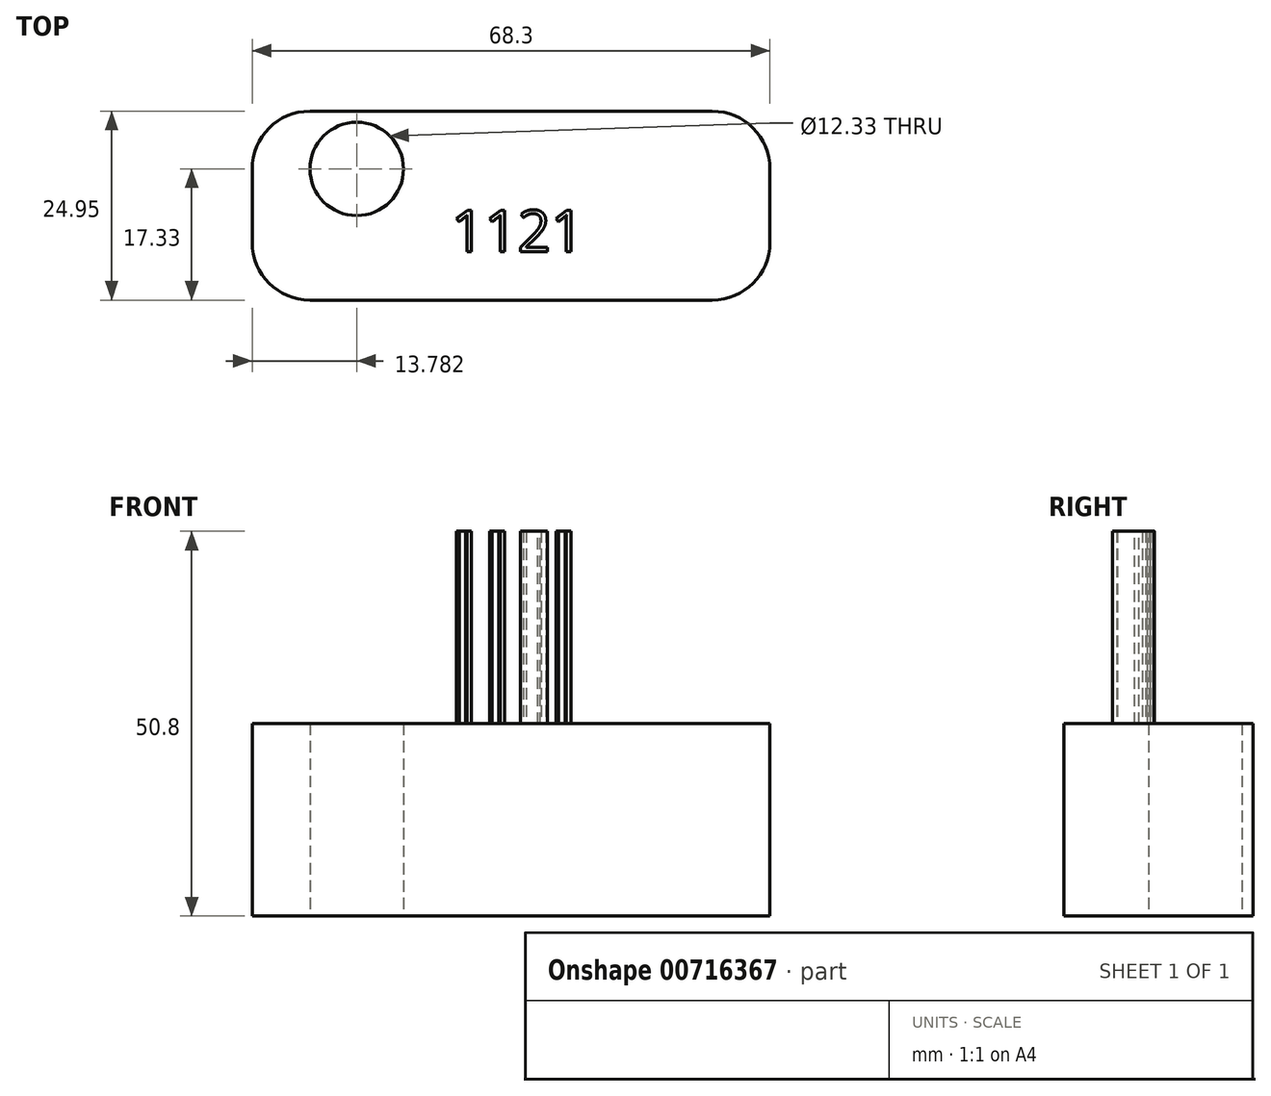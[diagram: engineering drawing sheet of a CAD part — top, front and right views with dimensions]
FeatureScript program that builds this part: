
annotation { "Feature Type Name" : "Feature", "Feature Type Description" : "" }
export const myFeature = defineFeature(function(context is Context, id is Id, definition is map)
    precondition{}
    {
        {
            var Q0;
            Q0=qCreatedBy(makeId("Top.planeOp"),FACE);
            var sketch = newSketch(context, id + "F0", { "sketchPlane" : qUnion([Q0])});
            skLineSegment(sketch, "E0.bottom", {"start": v(-7.62, 33.82) * mm, "end": v(-60.68, 33.82) * mm});
            skLineSegment(sketch, "E0.top", {"start": v(-7.62, 8.87) * mm, "end": v(-60.68, 8.87) * mm});
            skLineSegment(sketch, "E0.left", {"start": v(0, 26.2) * mm, "end": v(0, 16.49) * mm});
            skLineSegment(sketch, "E0.right", {"start": v(-68.3, 26.2) * mm, "end": v(-68.3, 16.49) * mm});
            skPoint(sketch, "E0.middle", {"position": v(-34.15, 21.34) * mm});
            skPoint(sketch, "E1.visualSharp", {"position": v(0, 33.82) * mm});
            skArc(sketch, "E1.filletArc", {"start": v(0, 26.2) * mm, "mid": v(-2.23, 31.59) * mm, "end": v(-7.62, 33.82) * mm});
            skPoint(sketch, "E2.visualSharp", {"position": v(0, 8.87) * mm});
            skArc(sketch, "E2.filletArc", {"start": v(-7.62, 8.87) * mm, "mid": v(-2.23, 11.1) * mm, "end": v(0, 16.49) * mm});
            skPoint(sketch, "E3.visualSharp", {"position": v(-68.3, 8.87) * mm});
            skArc(sketch, "E3.filletArc", {"start": v(-68.3, 16.49) * mm, "mid": v(-66.07, 11.1) * mm, "end": v(-60.68, 8.87) * mm});
            skPoint(sketch, "E4.visualSharp", {"position": v(-68.3, 33.82) * mm});
            skArc(sketch, "E4.filletArc", {"start": v(-60.68, 33.82) * mm, "mid": v(-66.07, 31.59) * mm, "end": v(-68.3, 26.2) * mm});
            skCircle(sketch, "E5", {"center": v(-54.52, 26.2) * mm, "radius": 6.17 * mm});
            skSolve(sketch);
        }
        {
            var Q0;
            Q0=makeQuery(id+"F0.imprint","IMPRINT",FACE,{"disambiguationData":[TD([[makeQuery(id+"F0.imprint","IMPRINT",EDGE,{"derivedFrom":sQuery(id+"F0.wireOp",EDGE,"E0.bottom")}),1.0]])]});
            extrude(context, id + "F1", {"entities" : qUnion([Q0]), "depth" : 25.4 * mm, "offsetDistance" : 25.4 * mm});
        }
        {
            var Q0;
            Q0=makeQuery(id+"F1.opExtrude","CAP_FACE",FACE,{"disambiguationData":[OSD([sQuery(id+"F0.wireOp",EDGE,"E0.bottom"),sQuery(id+"F0.wireOp",EDGE,"E0.top"),sQuery(id+"F0.wireOp",EDGE,"E0.left"),sQuery(id+"F0.wireOp",EDGE,"E0.right"),sQuery(id+"F0.wireOp",EDGE,"E1.filletArc"),sQuery(id+"F0.wireOp",EDGE,"E2.filletArc"),sQuery(id+"F0.wireOp",EDGE,"E3.filletArc"),sQuery(id+"F0.wireOp",EDGE,"E4.filletArc"),sQuery(id+"F0.wireOp",EDGE,"E5")])],"isStart":false});
            var sketch = newSketch(context, id + "F2", { "sketchPlane" : qUnion([Q0])});
            skText(sketch, "E6", { "text": "1121", "fontName": "OpenSans-Regular.ttf"});
            const initialGuessF2  = {"E6": [-0.04204, 0.01529, 1, 0, 0.0055]};
            skSetInitialGuess(sketch, initialGuessF2);
            skSolve(sketch);
        }
        {
            var Q0;
            Q0 = qSketchRegion(id + "F2", true);
            extrude(context, id + "F3", {"entities" : qUnion([Q0]), "operationType" : NewBodyOperationType.ADD, "depth" : 25.4 * mm, "offsetDistance" : 25.4 * mm});
        }
    });
